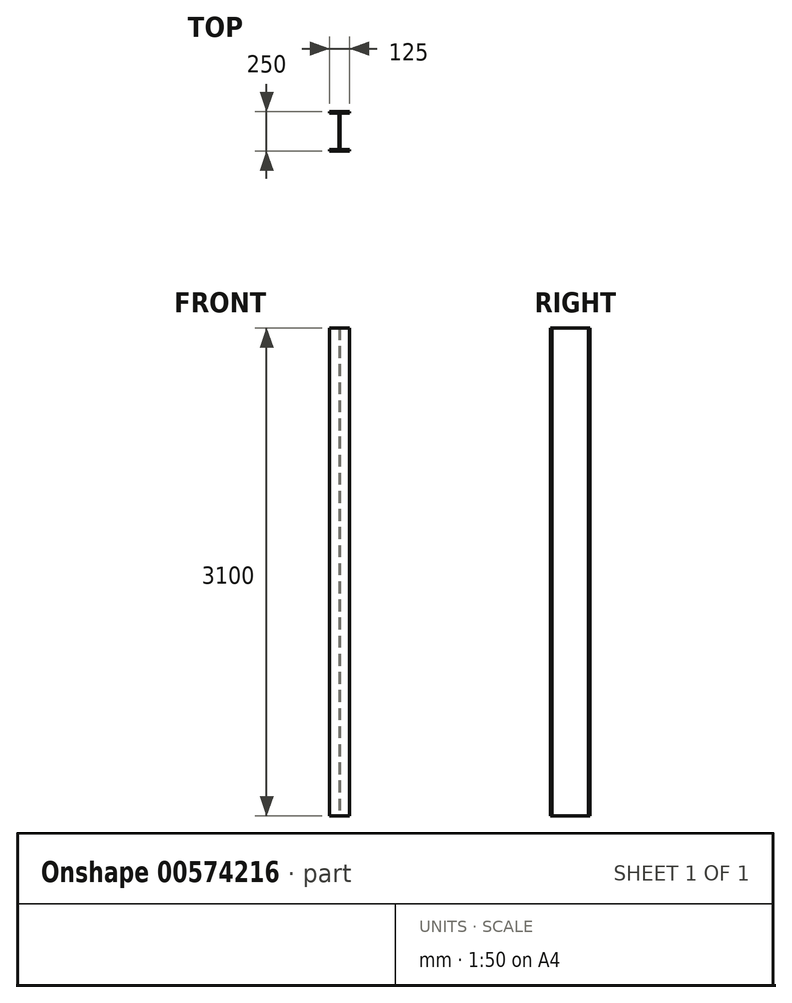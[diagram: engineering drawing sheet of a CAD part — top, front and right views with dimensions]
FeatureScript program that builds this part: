
annotation { "Feature Type Name" : "Feature", "Feature Type Description" : "" }
export const myFeature = defineFeature(function(context is Context, id is Id, definition is map)
    precondition{}
    {
        {
            var Q0;
            Q0=qCreatedBy(makeId("Top.planeOp"),FACE);
            var sketch = newSketch(context, id + "F0", { "sketchPlane" : qUnion([Q0])});
            skLineSegment(sketch, "E0", {"start": v(-33.92, 168.75) * mm, "end": v(-96.42, 168.75) * mm});
            skLineSegment(sketch, "E1", {"start": v(-96.42, 168.75) * mm, "end": v(-96.42, 159.75) * mm});
            skLineSegment(sketch, "E2", {"start": v(-96.42, 159.75) * mm, "end": v(-36.92, 159.75) * mm});
            skLineSegment(sketch, "E3", {"start": v(-36.92, 159.75) * mm, "end": v(-36.92, -72.25) * mm});
            skLineSegment(sketch, "E4", {"start": v(-36.92, -72.25) * mm, "end": v(-96.42, -72.25) * mm});
            skLineSegment(sketch, "E5", {"start": v(-96.42, -72.25) * mm, "end": v(-96.42, -81.25) * mm});
            skLineSegment(sketch, "E6", {"start": v(-96.42, -81.25) * mm, "end": v(-33.92, -81.25) * mm});
            skLineSegment(sketch, "E7.MirrorCS", {"start": v(28.58, 159.75) * mm, "end": v(-30.92, 159.75) * mm});
            skLineSegment(sketch, "E8.MirrorCS", {"start": v(28.58, -81.25) * mm, "end": v(-33.92, -81.25) * mm});
            skLineSegment(sketch, "E9.MirrorCS", {"start": v(-30.92, -72.25) * mm, "end": v(28.58, -72.25) * mm});
            skLineSegment(sketch, "E10.MirrorCS", {"start": v(28.58, -72.25) * mm, "end": v(28.58, -81.25) * mm});
            skLineSegment(sketch, "E11.MirrorCS", {"start": v(-30.92, 159.75) * mm, "end": v(-30.92, -72.25) * mm});
            skLineSegment(sketch, "E12.MirrorCS", {"start": v(-33.92, 168.75) * mm, "end": v(28.58, 168.75) * mm});
            skLineSegment(sketch, "E13.MirrorCS", {"start": v(28.58, 168.75) * mm, "end": v(28.58, 159.75) * mm});
            skSolve(sketch);
        }
        {
            var Q0;
            Q0=makeQuery(id+"F0.imprint","IMPRINT",FACE,{"disambiguationData":[TD([[makeQuery(id+"F0.imprint","IMPRINT",EDGE,{"derivedFrom":sQuery(id+"F0.wireOp",EDGE,"E0")}),1.0]])]});
            extrude(context, id + "F1", {"entities" : qUnion([Q0]), "depth" : 3100 * mm, "offsetDistance" : 25 * mm});
        }
    });
